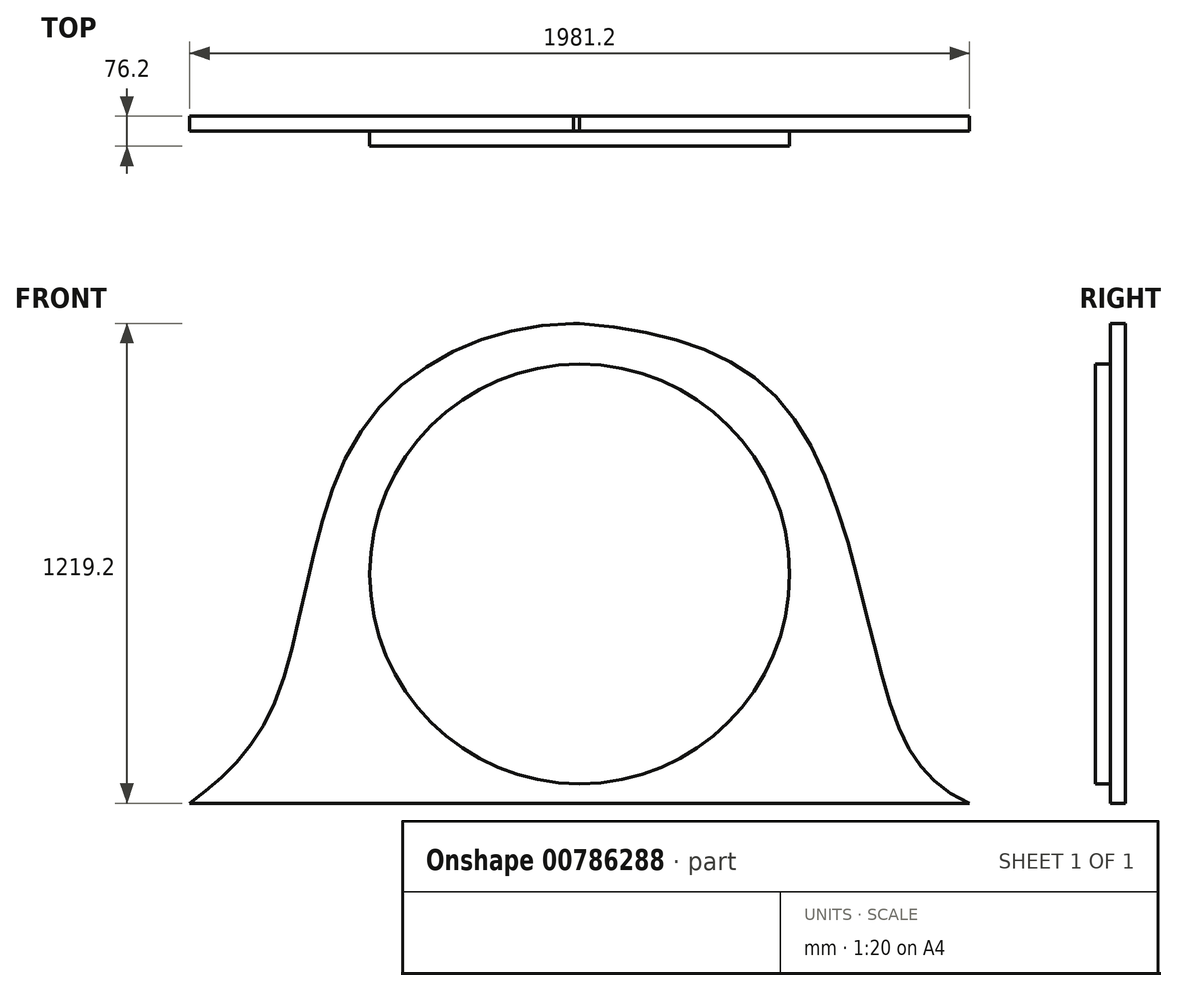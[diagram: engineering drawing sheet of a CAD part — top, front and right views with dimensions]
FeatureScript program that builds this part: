
annotation { "Feature Type Name" : "Feature", "Feature Type Description" : "" }
export const myFeature = defineFeature(function(context is Context, id is Id, definition is map)
    precondition{}
    {
        {
            var Q0;
            Q0=qCreatedBy(makeId("Front.planeOp"),FACE);
            var sketch = newSketch(context, id + "F0", { "sketchPlane" : qUnion([Q0])});
            skCircle(sketch, "E0", {"center": v(0, 0) * mm, "radius": 533.4 * mm});
            skLineSegment(sketch, "E1.bottom", {"start": v(-990.6, 636.72) * mm, "end": v(990.6, 636.72) * mm});
            skLineSegment(sketch, "E1.top", {"start": v(-990.6, -582.48) * mm, "end": v(990.6, -582.48) * mm});
            skLineSegment(sketch, "E1.left", {"start": v(-990.6, 636.72) * mm, "end": v(-990.6, -582.48) * mm});
            skLineSegment(sketch, "E1.right", {"start": v(990.6, 636.72) * mm, "end": v(990.6, -582.48) * mm});
            skFitSpline(sketch, "E2", {"points": [v(0, 636.72) * mm, v(-559.02, 357.68) * mm, v(-772.01, -320.43) * mm, v(-990.6, -582.48) * mm], "startDerivative": vector(-1842.38, 20.51) * mm, "endDerivative": vector(-945.08, -707.82) * mm});
            skFitSpline(sketch, "E3", {"points": [v(0, 636.72) * mm, v(549.44, 388.1) * mm, v(792.87, -342.17) * mm, v(990.6, -582.48) * mm], "startDerivative": vector(2043.94, -178.52) * mm, "endDerivative": vector(1212.13, -527.77) * mm});
            skSolve(sketch);
        }
        {
            var Q0;
            Q0=makeQuery(id+"F0.imprint","IMPRINT",FACE,{"disambiguationData":[TD([[makeQuery(id+"F0.imprint","IMPRINT",EDGE,{"derivedFrom":sQuery(id+"F0.wireOp",EDGE,"E0")}),1.0]])]});
            extrude(context, id + "F1", {"entities" : qUnion([Q0]), "depth" : 76.2 * mm, "offsetDistance" : 25.4 * mm});
        }
        {
            var Q0;
            Q0=makeQuery(id+"F0.imprint","IMPRINT",FACE,{"disambiguationData":[TD([[makeQuery(id+"F0.imprint","IMPRINT",EDGE,{"derivedFrom":sQuery(id+"F0.wireOp",EDGE,"E0")}),-1.0]])]});
            extrude(context, id + "F2", {"entities" : qUnion([Q0]), "operationType" : NewBodyOperationType.ADD, "depth" : 38.1 * mm, "offsetDistance" : 25.4 * mm});
        }
    });
